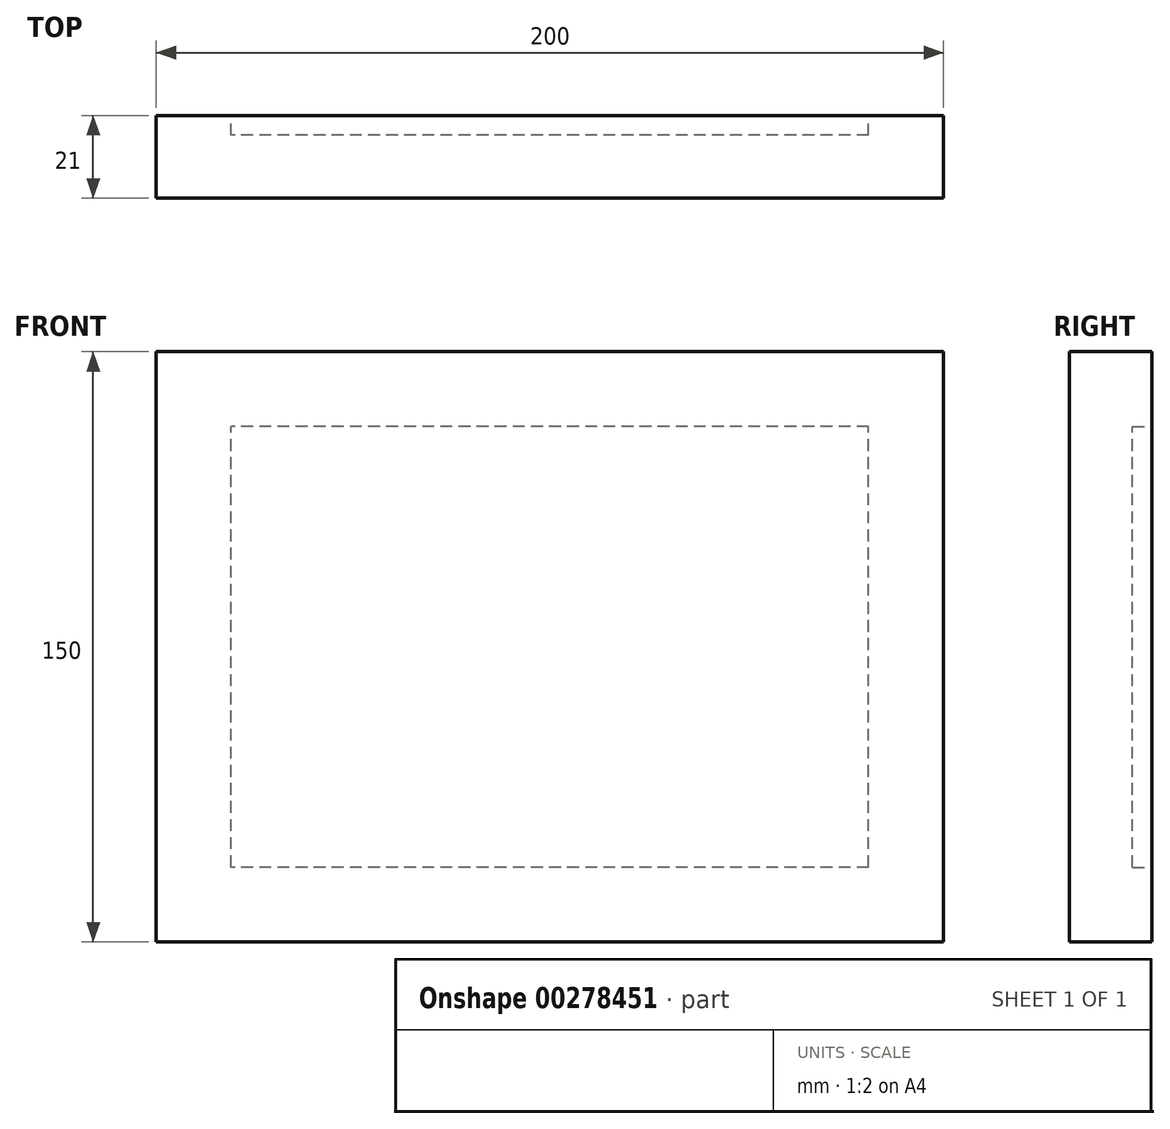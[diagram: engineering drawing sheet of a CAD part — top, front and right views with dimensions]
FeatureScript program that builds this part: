
annotation { "Feature Type Name" : "Feature", "Feature Type Description" : "" }
export const myFeature = defineFeature(function(context is Context, id is Id, definition is map)
    precondition{}
    {
        {
            var Q0;
            Q0=qCreatedBy(makeId("Front.planeOp"),FACE);
            var sketch = newSketch(context, id + "F0", { "sketchPlane" : qUnion([Q0])});
            skLineSegment(sketch, "E0.bottom", {"start": v(100, -75) * mm, "end": v(-100, -75) * mm});
            skLineSegment(sketch, "E0.top", {"start": v(100, 75) * mm, "end": v(-100, 75) * mm});
            skLineSegment(sketch, "E0.left", {"start": v(100, -75) * mm, "end": v(100, 75) * mm});
            skLineSegment(sketch, "E0.right", {"start": v(-100, -75) * mm, "end": v(-100, 75) * mm});
            skPoint(sketch, "E0.middle", {"position": v(0, 0) * mm});
            skLineSegment(sketch, "E1.0", {"start": v(81, 56) * mm, "end": v(-81, 56) * mm});
            skLineSegment(sketch, "E1.1", {"start": v(81, -56) * mm, "end": v(81, 56) * mm});
            skLineSegment(sketch, "E1.2", {"start": v(81, -56) * mm, "end": v(-81, -56) * mm});
            skLineSegment(sketch, "E1.3", {"start": v(-81, -56) * mm, "end": v(-81, 56) * mm});
            skSolve(sketch);
        }
        {
            var Q0;
            Q0=makeQuery(id+"F0.imprint","IMPRINT",FACE,{"disambiguationData":[TD([[makeQuery(id+"F0.imprint","IMPRINT",EDGE,{"derivedFrom":sQuery(id+"F0.wireOp",EDGE,"E0.bottom")}),-1.0]])]});
            var Q1;
            Q1=makeQuery(id+"F0.imprint","IMPRINT",FACE,{"disambiguationData":[TD([[makeQuery(id+"F0.imprint","IMPRINT",EDGE,{"derivedFrom":sQuery(id+"F0.wireOp",EDGE,"E1.0")}),1.0]])]});
            extrude(context, id + "F1", {"entities" : qUnion([Q0, Q1]), "depth" : 21 * mm});
        }
        {
            var Q0;
            Q0=makeQuery(id+"F0.imprint","IMPRINT",FACE,{"disambiguationData":[TD([[makeQuery(id+"F0.imprint","IMPRINT",EDGE,{"derivedFrom":sQuery(id+"F0.wireOp",EDGE,"E1.0")}),1.0]])]});
            extrude(context, id + "F2", {"entities" : qUnion([Q0]), "operationType" : NewBodyOperationType.REMOVE, "depth" : 5 * mm});
        }
    });
